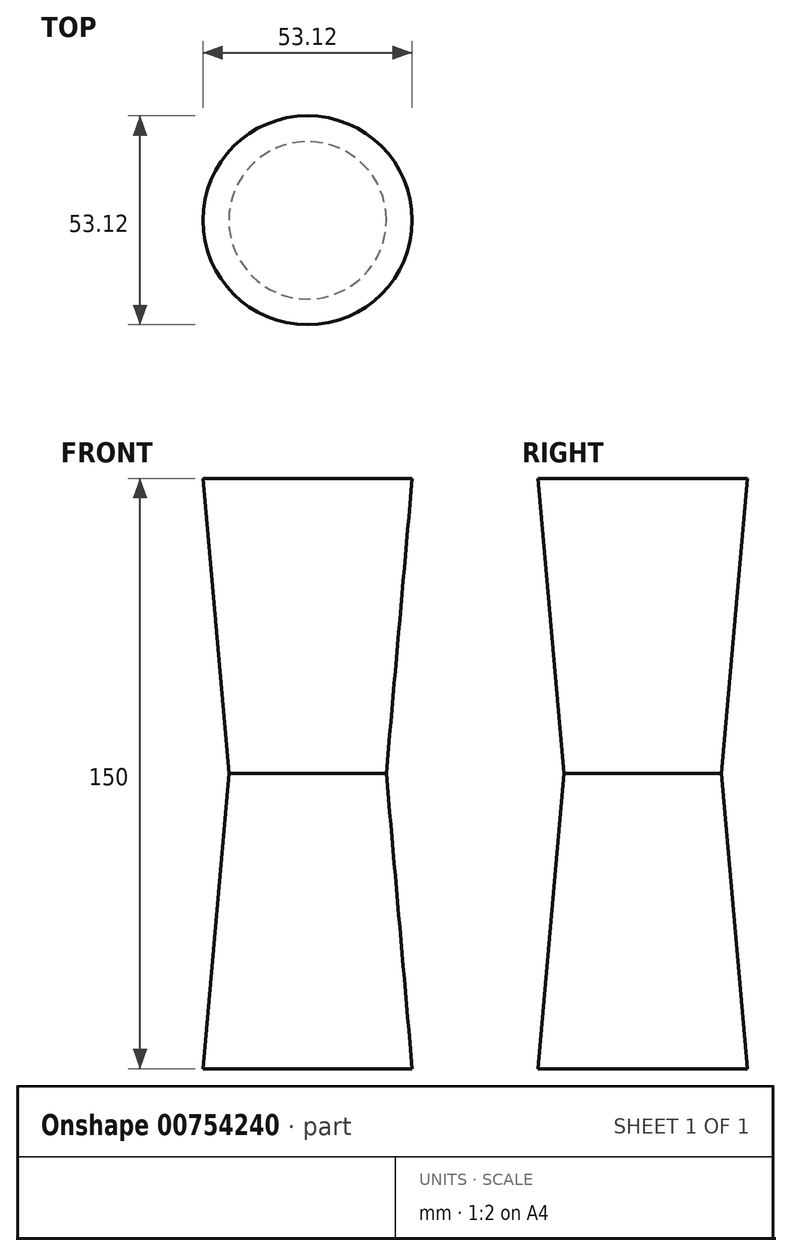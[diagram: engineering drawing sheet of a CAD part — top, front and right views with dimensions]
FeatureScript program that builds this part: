
annotation { "Feature Type Name" : "Feature", "Feature Type Description" : "" }
export const myFeature = defineFeature(function(context is Context, id is Id, definition is map)
    precondition{}
    {
        {
            var Q0;
            Q0=qCreatedBy(makeId("Top.planeOp"),FACE);
            var sketch = newSketch(context, id + "F0", { "sketchPlane" : qUnion([Q0])});
            skCircle(sketch, "E0", {"center": v(0, 0) * mm, "radius": 20 * mm});
            skSolve(sketch);
        }
        {
            var Q0;
            Q0 = qSketchRegion(id + "F0", true);
            extrude(context, id + "F1", {"entities" : qUnion([Q0]), "endBound" : BoundingType.SYMMETRIC, "depth" : 150 * mm, "offsetDistance" : 25 * mm, "hasDraft" : true, "draftAngle" : 5 * degree});
        }
    });
